# Revit family: Titus-CBAL2 - 24 Wide, Active Chilled Beam, Revit 2018, R1.0a
name_source: partatom
category: Mechanical Equipment
revit_build: Autodesk Revit 2018 (Build: 20170630_0700(x64)
units: mm (PartAtom-declared; Revit-internal decimal feet)

## family parameters
Cut with Voids When Loaded = Yes
Host = Face
OmniClass Number = 23.75.70.17.31
OmniClass Title = Induction Units
Part Type = Normal
Room Calculation Point = No
Round Connector Dimension = Use Radius
Shared = No

## types (1)
- CBAL2-24
    10 Feet = No
    10" Oval = No
    2 - Two-way,Throw = Yes
    2 Feet = No
    2-Pipe System = No
    24" Wide Beam = Yes
    26 - White = Yes
    2P1C - 2 Pipe, 1 Coil Circuit = No
    2P2C - 2 Pipe, 2 Coil Circuit = No
    3 - LAY-IN = Yes
    3 Feet = No
    3PT - 3/4" Male Pipe Thread = No
    4 Feet = No
    4" Dia. = No
    4-Pipe System = Yes
    4P1C - 4 Pipe, 1 Coil Circuit = No
    4P2C - 4 Pipe, 2 Coil Circuit = Yes
    5 Feet = Yes
    5" Dia. = No
    6 Feet = No
    6" Dia. = Yes
    7 Feet = No
    8 Feet = No
    8" Oval = No
    9 Feet = No
    A = 7"
    Actual Coefficient of Performance = 0
    Actual Cooling Entering Dry Bulb Temperature = 0 °F
    Actual Cooling Entering Wet Bulb Temperature = 0 °F
    Actual Cooling Leaving Dry Bulb Temperature = 0 °F
    Actual Cooling Leaving Wet Bulb Temperature = 0 °F
    Actual Energy Efficiency Rating (BTU/h.W) = 0
    Actual External Static Pressure = 0.00 in-wg
    Actual Filter Face Area = 0 SF
    Actual Full Load Efficiency = 0
    Actual Heating Entering Dry Bulb Temperature = 0 °F
    Actual Heating Leaving Dry Bulb Temperature = 0 °F
    Actual Height = 8 3/8"
    Actual Oval Width = 9 3/8"
    Actual Oval height = 5 1/4"
    Actual Radius = 2 15/16"
    Actual Total Static Pressure = 0.00 in-wg
    B - One-way, Back = No
    CTRL Angle = 90.00°
    CTRL Multi-Inlet Angle = 0.00°
    CTRL Multi-Inlet Connector Offset = 6 5/64"
    CTRL Multi-Inlet Offset = 5"
    CTRL Multi-Inlet Oval Angle = 0.00°
    CTRL Multi-Inlet Oval Connector Offset = 6 5/64"
    CTRL Multi-Inlet Round Angle = 0.00°
    CTRL Multi-Inlet Round Connector Offset = 6 5/64"
    CTRL Offset = 0"
    CTRL Oval Connector Offset = 4"
    CTRL Perforation Hole Dia = 1/8"
    CTRL Perforation Offset = 1/2"
    CTRL Pipe Connector Offset = 1 43/64"
    CTRL Round Connector Offset = 0"
    CTRL Thickness = 1/16"
    CWR Ver Offset = 7 1/8"
    CWS Ver Offset = 7 3/4"
    Coil Material = JCI - Metal - Copper
    Condenser Inlet Radius = 1/4"
    Condenser Outlet Radius = 1/4"
    Condenser Pressure Drop = 0.00 psi
    Condenser Refrigerant Inlet Description = Condenser Refrigerant Inlet
    Condenser Refrigerant Outlet Description = Condenser Refrigerant Outlet
    Conditioned Air (Oval) Description = Disabled
    Conditioned Air (Round) Description = Conditioned Air
    Conditioned Air Connection Height = 1/2"
    Conditioned Air Connection Radius = 3"
    Conditioned Air Connection Width = 1/2"
    Connector Offset = 6 5/64"
    Default Elevation = 0"
    Description = Active Chilled Beam Diffuser, Ceiling Mounted
    Design Ambient Summer Dry Bulb Temperature = 0 °F
    Design Ambient Winter Dry Bulb Temperature = 0 °F
    Design Ambient summer Wet bulb Temperature = 0 °F
    Design Cooling Minimum Air Flow = 0 CFM
    Design Heating Maximum Air Flow = 0 CFM
    Design Heating Minimum Air Flow = 0 CFM
    Design cooling Maximum Air Flow = 0 CFM
    Evaporator Inlet Radius = 1/4"
    Evaporator Outlet Radius = 1/4"
    Evaporator Pressure Drop = 0.00 psi
    Evaporator Refrigerant Inlet Description = Evaporator Refrigerant Inlet
    Evaporator Refrigerant Outlet Description = Evaporator Refrigerant Outlet
    F - One-way, Front = No
    Frame Extension = 3/8"
    H12 - SS Flex Hose - 12in = No
    H18 - SS Flex Hose - 18in = No
    H24 - SS Flex Hose - 24in = No
    HWR Ver Offset = 9 5/8"
    HWS Ver Offset = 10 1/4"
    Hanger Dimension A = 7"
    Height = 10 1/8"
    Hor Chilled Water Return Offset = 7 1/8"
    Hor Chilled Water Supply Offset = 7 3/4"
    Hor Hot Water Return Offset = 2 1/2"
    Hor Hot Water Supply Offset = 2 1/2"
    Inner Length = 59 3/8"
    Inner Width = 23 3/8"
    Input your Special Finish's name = Input your Special Finish's name
    Lay In Width = 23 3/4"
    M13 = Yes
    M17 = No
    M20 = No
    M23 = No
    M27 = No
    M31 = No
    MPT - 1/2" Male Pipe Thread = No
    Manufacturer = Titus HVAC
    Material = JCI - Metal - Steel - Galvanized
    Model = CBAL2-24
    Multi-Inlet = No
    NT - Tegular 9/16 Inch = No
    Pipe Connections Left Hand = Yes
    Pipe Connections Right Hand = No
    Pipe Height = 6"
    Primary Air Extension = 2 5/8"
    Primary Air Ver Offset = 6 1/8"
    SWT - Sweat = Yes
    Select Border Type = 1
    Select a Beam Length = 4
    Select a Piping Connection Type = 1
    Select a Water Coil Connection = 1
    Select a Water-Coil Type = 4
    Select an Air Inlet Dia = 3
    Select an Air Inlet Location = 2
    Select an Air Nozzle Configuration = 1
    Select an Air Throw Pattern = 1
    Select an Exposed Face Finish = 1
    Show Oval Connector = No
    Show Room Tag = No
    Show Round Connector = Yes
    Side Middle = No
    Side Plate = No
    Special Finish = No
    Top Middle = Yes
    Top Plate = Yes
    Total Length = 59 3/4"
    Total Width = 23 3/4"

## geometry (parser evidence)
native form markers: Sweep x25
no freeform markers — native parametric forms only
